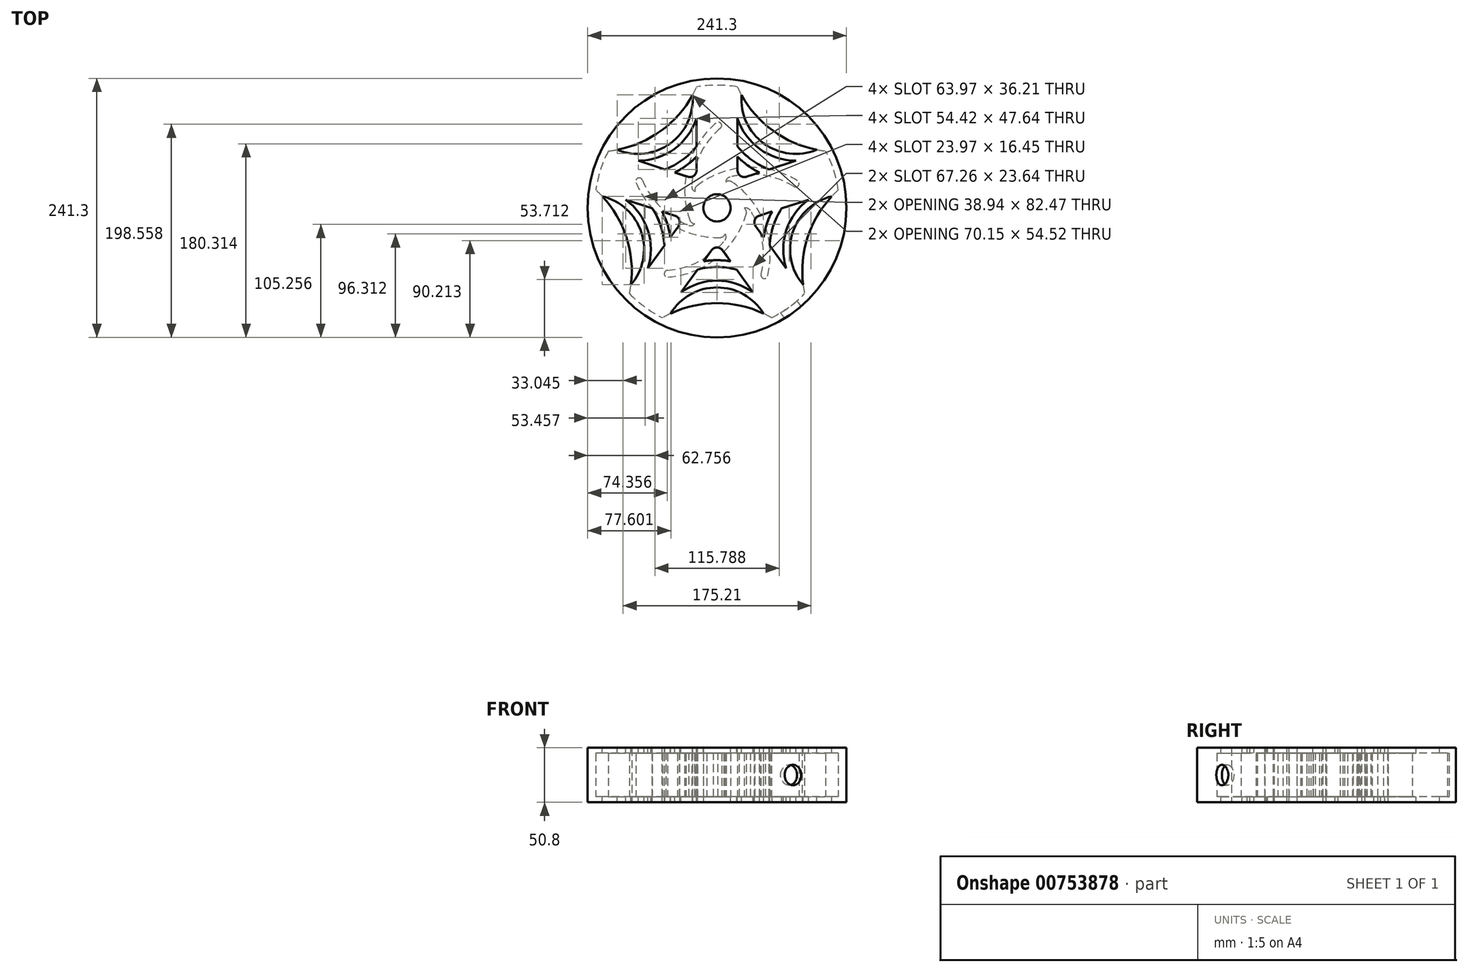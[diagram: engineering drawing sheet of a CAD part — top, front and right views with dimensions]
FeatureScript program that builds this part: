
annotation { "Feature Type Name" : "Feature", "Feature Type Description" : "" }
export const myFeature = defineFeature(function(context is Context, id is Id, definition is map)
    precondition{}
    {
        {
            var Q0;
            Q0=qCreatedBy(makeId("Top.planeOp"),FACE);
            var sketch = newSketch(context, id + "F0", { "sketchPlane" : qUnion([Q0])});
            skCircle(sketch, "E0", {"center": v(0, 0) * mm, "radius": 120.65 * mm});
            skArc(sketch, "E1.0", {"start": v(50.8, -102.4) * mm, "mid": v(67.18, -92.47) * mm, "end": v(81.68, -79.95) * mm});
            skLineSegment(sketch, "E2", {"start": v(0, 0) * mm, "end": v(0, -114.3) * mm, "construction": true});
            skArc(sketch, "E3", {"start": v(50.8, -102.4) * mm, "mid": v(0, -88.78) * mm, "end": v(-50.8, -102.4) * mm});
            skLineSegment(sketch, "E4", {"start": v(50.8, -102.4) * mm, "end": v(0, -102.4) * mm, "construction": true});
            skLineSegment(sketch, "E5", {"start": v(0, -102.4) * mm, "end": v(-50.8, -102.4) * mm, "construction": true});
            skArc(sketch, "E6.1.0", {"start": v(113.08, 16.67) * mm, "mid": v(84.43, -27.43) * mm, "end": v(81.68, -79.95) * mm});
            skArc(sketch, "E6.2.0", {"start": v(19.09, 112.7) * mm, "mid": v(52.18, 71.82) * mm, "end": v(101.28, 52.98) * mm});
            skArc(sketch, "E6.3.0", {"start": v(-101.28, 52.98) * mm, "mid": v(-52.18, 71.82) * mm, "end": v(-19.09, 112.7) * mm});
            skArc(sketch, "E6.4.0", {"start": v(-81.68, -79.95) * mm, "mid": v(-84.43, -27.43) * mm, "end": v(-113.08, 16.67) * mm});
            skArc(sketch, "E7.trimOffspring", {"start": v(113.08, 16.67) * mm, "mid": v(108.7, 35.32) * mm, "end": v(101.28, 52.98) * mm});
            skArc(sketch, "E8.trimOffspring", {"start": v(-81.68, -79.95) * mm, "mid": v(-67.18, -92.47) * mm, "end": v(-50.8, -102.4) * mm});
            skArc(sketch, "E9.trimOffspring", {"start": v(-101.28, 52.98) * mm, "mid": v(-108.7, 35.32) * mm, "end": v(-113.08, 16.67) * mm});
            skArc(sketch, "E10.trimOffspring", {"start": v(19.09, 112.7) * mm, "mid": v(0, 114.3) * mm, "end": v(-19.09, 112.7) * mm});
            skSolve(sketch);
        }
        {
            var Q0;
            Q0=makeQuery(id+"F0.imprint","IMPRINT",FACE,{"disambiguationData":[TD([[makeQuery(id+"F0.imprint","IMPRINT",EDGE,{"derivedFrom":sQuery(id+"F0.wireOp",EDGE,"E1.0")}),1.0]])]});
            var Q1;
            Q1=makeQuery(id+"F0.imprint","IMPRINT",FACE,{"disambiguationData":[TD([[makeQuery(id+"F0.imprint","IMPRINT",EDGE,{"derivedFrom":sQuery(id+"F0.wireOp",EDGE,"E0")}),1.0]])]});
            extrude(context, id + "F1", {"entities" : qUnion([Q0, Q1]), "depth" : 50.8 * mm, "offsetDistance" : 25.4 * mm, "symmetric" : true});
        }
        {
            var Q0;
            Q0=makeQuery(id+"F0.imprint","IMPRINT",FACE,{"disambiguationData":[TD([[makeQuery(id+"F0.imprint","IMPRINT",EDGE,{"derivedFrom":sQuery(id+"F0.wireOp",EDGE,"E1.0")}),1.0]])]});
            extrude(context, id + "F2", {"entities" : qUnion([Q0]), "operationType" : NewBodyOperationType.REMOVE, "depth" : 40.64 * mm, "offsetDistance" : 25.4 * mm, "symmetric" : true});
        }
        {
            var Q0;
            Q0=makeQuery(id+"F1.opExtrude","CAP_FACE",FACE,{"disambiguationData":[OSD([sQuery(id+"F0.wireOp",EDGE,"E0")])],"isStart":false});
            var sketch = newSketch(context, id + "F3", { "sketchPlane" : qUnion([Q0])});
            skCircle(sketch, "E11", {"center": v(0, 0) * mm, "radius": 12.7 * mm});
            skSolve(sketch);
        }
        {
            var Q0;
            Q0=makeQuery(id+"F3.imprint","IMPRINT",FACE,{"disambiguationData":[TD([[makeQuery(id+"F3.imprint","IMPRINT",EDGE,{"derivedFrom":sQuery(id+"F3.wireOp",EDGE,"E11")}),1.0]])]});
            extrude(context, id + "F4", {"entities" : qUnion([Q0]), "operationType" : NewBodyOperationType.REMOVE, "oppositeDirection" : true, "depth" : 25.4 * mm, "offsetDistance" : 25.4 * mm});
        }
        {
            var Q0;
            Q0=makeQuery(id+"F2.boolean.opBoolean","COPY",VERTEX,{"derivedFrom":makeQuery(id+"F2.opExtrude","CAP_VERTEX",VERTEX,{"disambiguationData":[OSD([sQuery(id+"F0.wireOp",EDGE,"E1.0"),sQuery(id+"F0.wireOp",EDGE,"E3")])],"isStart":true})});
            var Q1;
            Q1=makeQuery(id+"F2.boolean.opBoolean","COPY",VERTEX,{"derivedFrom":makeQuery(id+"F2.opExtrude","CAP_VERTEX",VERTEX,{"disambiguationData":[OSD([sQuery(id+"F0.wireOp",EDGE,"E1.0"),sQuery(id+"F0.wireOp",EDGE,"E6.1.0")])],"isStart":true})});
            var Q2;
            Q2=makeQuery(id+"F2.boolean.opBoolean","COPY",VERTEX,{"derivedFrom":makeQuery(id+"F2.opExtrude","CAP_VERTEX",VERTEX,{"disambiguationData":[OSD([sQuery(id+"F0.wireOp",EDGE,"E1.0"),sQuery(id+"F0.wireOp",EDGE,"E6.1.0")])],"isStart":false})});
            cPlane(context, id + "F5", {"entities" : qUnion([Q0, Q1, Q2]), "cplaneType" : CPlaneType.THREE_POINT, "offset" : 25.4 * mm, "width" : 152.4 * mm, "height" : 152.4 * mm});
        }
        {
            var Q0;
            Q0=qCreatedBy(id+"F5.planeOp",FACE);
            var sketch = newSketch(context, id + "F6", { "sketchPlane" : qUnion([Q0])});
            skCircle(sketch, "E12", {"center": v(0, 0) * mm, "radius": 9.53 * mm});
            skSolve(sketch);
        }
        {
            var Q0;
            Q0 = qSketchRegion(id + "F6", true);
            extrude(context, id + "F7", {"entities" : qUnion([Q0]), "operationType" : NewBodyOperationType.REMOVE, "oppositeDirection" : true, "depth" : 25.4 * mm, "offsetDistance" : 25.4 * mm});
        }
        {
            var Q0;
            Q0=qCreatedBy(makeId("Top.planeOp"),FACE);
            var sketch = newSketch(context, id + "F8", { "sketchPlane" : qUnion([Q0])});
            skCircle(sketch, "E13", {"center": v(0, 0) * mm, "radius": 12.7 * mm});
            skArc(sketch, "E14.0", {"start": v(7.62, -24.23) * mm, "mid": v(10.53, -23.11) * mm, "end": v(13.29, -21.65) * mm});
            skLineSegment(sketch, "E15", {"start": v(13.29, -21.65) * mm, "end": v(-81.68, -79.95) * mm, "construction": true});
            skArc(sketch, "E16", {"start": v(-46.24, -58.2) * mm, "mid": v(-12.04, -47.14) * mm, "end": v(13.29, -21.65) * mm});
            skArc(sketch, "E17.0", {"start": v(-45.76, -64.52) * mm, "mid": v(2.06, -44.67) * mm, "end": v(28.65, -0.24) * mm});
            skLineSegment(sketch, "E18", {"start": v(28.65, -0.24) * mm, "end": v(25.4, -0.24) * mm});
            skArc(sketch, "E19", {"start": v(-46.24, -58.2) * mm, "mid": v(-49.17, -61.6) * mm, "end": v(-45.76, -64.52) * mm});
            skArc(sketch, "E20.1.0", {"start": v(41.06, -61.96) * mm, "mid": v(43.39, -65.8) * mm, "end": v(47.23, -63.46) * mm});
            skArc(sketch, "E20.1.1", {"start": v(41.06, -61.96) * mm, "mid": v(41.11, -26.02) * mm, "end": v(24.7, 5.95) * mm});
            skArc(sketch, "E20.1.2", {"start": v(47.23, -63.46) * mm, "mid": v(43.12, -11.85) * mm, "end": v(9.08, 27.17) * mm});
            skLineSegment(sketch, "E20.1.3", {"start": v(9.08, 27.17) * mm, "end": v(8.08, 24.08) * mm});
            skArc(sketch, "E20.2.0", {"start": v(71.61, 19.9) * mm, "mid": v(75.98, 20.93) * mm, "end": v(74.95, 25.3) * mm});
            skArc(sketch, "E20.2.1", {"start": v(71.61, 19.9) * mm, "mid": v(37.45, 31.06) * mm, "end": v(1.97, 25.32) * mm});
            skArc(sketch, "E20.2.2", {"start": v(74.95, 25.3) * mm, "mid": v(24.6, 37.35) * mm, "end": v(-23.03, 17.03) * mm});
            skLineSegment(sketch, "E20.2.3", {"start": v(-23.03, 17.03) * mm, "end": v(-20.4, 15.12) * mm});
            skArc(sketch, "E20.3.0", {"start": v(3.2, 74.26) * mm, "mid": v(3.57, 78.73) * mm, "end": v(-0.9, 79.1) * mm});
            skArc(sketch, "E20.3.1", {"start": v(3.2, 74.26) * mm, "mid": v(-17.97, 45.21) * mm, "end": v(-23.47, 9.7) * mm});
            skArc(sketch, "E20.3.2", {"start": v(-0.9, 79.1) * mm, "mid": v(-27.92, 34.93) * mm, "end": v(-23.32, -16.64) * mm});
            skLineSegment(sketch, "E20.3.3", {"start": v(-23.32, -16.64) * mm, "end": v(-20.69, -14.73) * mm});
            skArc(sketch, "E20.4.0", {"start": v(-69.63, 26) * mm, "mid": v(-73.77, 27.73) * mm, "end": v(-75.5, 23.58) * mm});
            skArc(sketch, "E20.4.1", {"start": v(-69.63, 26) * mm, "mid": v(-48.55, -3.12) * mm, "end": v(-16.48, -19.33) * mm});
            skArc(sketch, "E20.4.2", {"start": v(-75.5, 23.58) * mm, "mid": v(-41.85, -15.76) * mm, "end": v(8.62, -27.32) * mm});
            skLineSegment(sketch, "E20.4.3", {"start": v(8.62, -27.32) * mm, "end": v(7.62, -24.23) * mm});
            skArc(sketch, "E21.trimOffspring", {"start": v(-20.69, -14.73) * mm, "mid": v(-18.73, -17.16) * mm, "end": v(-16.48, -19.33) * mm});
            skArc(sketch, "E22.trimOffspring", {"start": v(-20.4, 15.12) * mm, "mid": v(-22.1, 12.5) * mm, "end": v(-23.47, 9.7) * mm});
            skArc(sketch, "E23.trimOffspring", {"start": v(8.08, 24.08) * mm, "mid": v(5.06, 24.9) * mm, "end": v(1.97, 25.32) * mm});
            skArc(sketch, "E24.trimOffspring", {"start": v(25.4, -0.24) * mm, "mid": v(25.24, 2.88) * mm, "end": v(24.7, 5.95) * mm});
            skSolve(sketch);
        }
        {
            var Q0;
            Q0 = qSketchRegion(id + "F8", true);
            extrude(context, id + "F9", {"entities" : qUnion([Q0]), "depth" : 40.64 * mm, "offsetDistance" : 25.4 * mm, "symmetric" : true});
        }
        {
            var Q0;
            Q0=makeQuery(id+"F9.opExtrude","SWEPT_EDGE",EDGE,{"disambiguationData":[OSD([sQuery(id+"F8.wireOp",EDGE,"E20.2.2"),sQuery(id+"F8.wireOp",EDGE,"E20.2.3")])]});
            var Q1;
            Q1=makeQuery(id+"F9.opExtrude","SWEPT_EDGE",EDGE,{"disambiguationData":[OSD([sQuery(id+"F8.wireOp",EDGE,"E20.3.1"),sQuery(id+"F8.wireOp",EDGE,"E22.trimOffspring")])]});
            var Q2;
            Q2=makeQuery(id+"F9.opExtrude","SWEPT_EDGE",EDGE,{"disambiguationData":[OSD([sQuery(id+"F8.wireOp",EDGE,"E20.3.2"),sQuery(id+"F8.wireOp",EDGE,"E20.3.3")])]});
            var Q3;
            Q3=makeQuery(id+"F9.opExtrude","SWEPT_EDGE",EDGE,{"disambiguationData":[OSD([sQuery(id+"F8.wireOp",EDGE,"E20.4.2"),sQuery(id+"F8.wireOp",EDGE,"E20.4.3")])]});
            var Q4;
            Q4=makeQuery(id+"F9.opExtrude","SWEPT_EDGE",EDGE,{"disambiguationData":[OSD([sQuery(id+"F8.wireOp",EDGE,"E17.0"),sQuery(id+"F8.wireOp",EDGE,"E18")])]});
            var Q5;
            Q5=makeQuery(id+"F9.opExtrude","SWEPT_EDGE",EDGE,{"disambiguationData":[OSD([sQuery(id+"F8.wireOp",EDGE,"E20.1.2"),sQuery(id+"F8.wireOp",EDGE,"E20.1.3")])]});
            var Q6;
            Q6=makeQuery(id+"F9.opExtrude","SWEPT_EDGE",EDGE,{"disambiguationData":[OSD([sQuery(id+"F8.wireOp",EDGE,"E20.4.1"),sQuery(id+"F8.wireOp",EDGE,"E21.trimOffspring")])]});
            var Q7;
            Q7=makeQuery(id+"F9.opExtrude","SWEPT_EDGE",EDGE,{"disambiguationData":[OSD([sQuery(id+"F8.wireOp",EDGE,"E14.0"),sQuery(id+"F8.wireOp",EDGE,"E16")])]});
            var Q8;
            Q8=makeQuery(id+"F9.opExtrude","SWEPT_EDGE",EDGE,{"disambiguationData":[OSD([sQuery(id+"F8.wireOp",EDGE,"E20.1.1"),sQuery(id+"F8.wireOp",EDGE,"E24.trimOffspring")])]});
            var Q9;
            Q9=makeQuery(id+"F9.opExtrude","SWEPT_EDGE",EDGE,{"disambiguationData":[OSD([sQuery(id+"F8.wireOp",EDGE,"E20.2.1"),sQuery(id+"F8.wireOp",EDGE,"E23.trimOffspring")])]});
            fillet(context, id + "F10", {"entities" : qUnion([Q0, Q1, Q2, Q3, Q4, Q5, Q6, Q7, Q8, Q9]), "radius" : 5.08 * mm, "tangentPropagation" : true, "allowEdgeOverflow" : false});
        }
        {
            var Q0;
            Q0=qCreatedBy(makeId("Top.planeOp"),FACE);
            var sketch = newSketch(context, id + "F11", { "sketchPlane" : qUnion([Q0])});
            skLineSegment(sketch, "E25", {"start": v(-5.14, -39.54) * mm, "end": v(-12.6, -49.82) * mm});
            skLineSegment(sketch, "E26.1.1", {"start": v(5.14, -39.54) * mm, "end": v(12.6, -49.82) * mm});
            skPoint(sketch, "E27.visualSharp", {"position": v(0, -32.47) * mm});
            skArc(sketch, "E27.filletArc", {"start": v(5.14, -39.54) * mm, "mid": v(0, -36.92) * mm, "end": v(-5.14, -39.54) * mm});
            skArc(sketch, "E28", {"start": v(12.6, -49.82) * mm, "mid": v(0, -48.77) * mm, "end": v(-12.6, -49.82) * mm});
            skArc(sketch, "E29.0", {"start": v(18.2, -57.53) * mm, "mid": v(0, -55.12) * mm, "end": v(-18.2, -57.53) * mm});
            skArc(sketch, "E30.0", {"start": v(33.63, -78.76) * mm, "mid": v(0, -67.82) * mm, "end": v(-33.63, -78.76) * mm});
            skArc(sketch, "E31.0", {"start": v(43.36, -98.5) * mm, "mid": v(0, -74.17) * mm, "end": v(-43.36, -98.5) * mm});
            skArc(sketch, "E32", {"start": v(43.36, -98.5) * mm, "mid": v(0, -88.78) * mm, "end": v(-43.36, -98.5) * mm});
            skLineSegment(sketch, "E33.trimOffspring", {"start": v(18.2, -57.53) * mm, "end": v(33.63, -78.76) * mm});
            skLineSegment(sketch, "E34.trimOffspring", {"start": v(-18.2, -57.53) * mm, "end": v(-33.63, -78.76) * mm});
            skArc(sketch, "E35.1.0", {"start": v(107.07, 10.8) * mm, "mid": v(84.43, -27.43) * mm, "end": v(80.28, -71.67) * mm});
            skArc(sketch, "E35.1.1", {"start": v(107.07, 10.8) * mm, "mid": v(70.54, -22.92) * mm, "end": v(80.28, -71.67) * mm});
            skArc(sketch, "E35.1.2", {"start": v(85.3, 7.65) * mm, "mid": v(64.5, -20.96) * mm, "end": v(64.51, -56.32) * mm});
            skLineSegment(sketch, "E35.1.3", {"start": v(60.34, -0.46) * mm, "end": v(85.3, 7.65) * mm});
            skLineSegment(sketch, "E35.1.4", {"start": v(49.09, -35.1) * mm, "end": v(64.51, -56.32) * mm});
            skArc(sketch, "E35.1.5", {"start": v(60.34, -0.46) * mm, "mid": v(52.42, -17.03) * mm, "end": v(49.09, -35.1) * mm});
            skArc(sketch, "E35.1.6", {"start": v(51.27, -3.4) * mm, "mid": v(46.38, -15.07) * mm, "end": v(43.48, -27.38) * mm});
            skLineSegment(sketch, "E35.1.7", {"start": v(39.2, -7.33) * mm, "end": v(51.27, -3.4) * mm});
            skLineSegment(sketch, "E35.1.8", {"start": v(36.02, -17.1) * mm, "end": v(43.48, -27.38) * mm});
            skArc(sketch, "E35.1.9", {"start": v(39.2, -7.33) * mm, "mid": v(35.12, -11.41) * mm, "end": v(36.02, -17.1) * mm});
            skArc(sketch, "E35.2.0", {"start": v(22.82, 105.17) * mm, "mid": v(52.18, 71.82) * mm, "end": v(92.97, 54.2) * mm});
            skArc(sketch, "E35.2.1", {"start": v(22.82, 105.17) * mm, "mid": v(43.6, 60) * mm, "end": v(92.97, 54.2) * mm});
            skArc(sketch, "E35.2.2", {"start": v(19.09, 83.49) * mm, "mid": v(39.86, 54.86) * mm, "end": v(73.5, 43.95) * mm});
            skLineSegment(sketch, "E35.2.3", {"start": v(19.09, 57.25) * mm, "end": v(19.09, 83.49) * mm});
            skLineSegment(sketch, "E35.2.4", {"start": v(48.55, 35.84) * mm, "end": v(73.5, 43.95) * mm});
            skArc(sketch, "E35.2.5", {"start": v(19.09, 57.25) * mm, "mid": v(32.4, 44.6) * mm, "end": v(48.55, 35.84) * mm});
            skArc(sketch, "E35.2.6", {"start": v(19.09, 47.7) * mm, "mid": v(28.66, 39.45) * mm, "end": v(39.48, 32.9) * mm});
            skLineSegment(sketch, "E35.2.7", {"start": v(19.09, 35) * mm, "end": v(19.09, 47.7) * mm});
            skLineSegment(sketch, "E35.2.8", {"start": v(27.4, 28.97) * mm, "end": v(39.48, 32.9) * mm});
            skArc(sketch, "E35.2.9", {"start": v(19.09, 35) * mm, "mid": v(21.7, 29.87) * mm, "end": v(27.4, 28.97) * mm});
            skArc(sketch, "E35.3.0", {"start": v(-92.97, 54.2) * mm, "mid": v(-52.18, 71.82) * mm, "end": v(-22.82, 105.17) * mm});
            skArc(sketch, "E35.3.1", {"start": v(-92.97, 54.2) * mm, "mid": v(-43.6, 60) * mm, "end": v(-22.82, 105.17) * mm});
            skArc(sketch, "E35.3.2", {"start": v(-73.5, 43.95) * mm, "mid": v(-39.86, 54.86) * mm, "end": v(-19.09, 83.49) * mm});
            skLineSegment(sketch, "E35.3.3", {"start": v(-48.55, 35.84) * mm, "end": v(-73.5, 43.95) * mm});
            skLineSegment(sketch, "E35.3.4", {"start": v(-19.09, 57.25) * mm, "end": v(-19.09, 83.49) * mm});
            skArc(sketch, "E35.3.5", {"start": v(-48.55, 35.84) * mm, "mid": v(-32.4, 44.6) * mm, "end": v(-19.09, 57.25) * mm});
            skArc(sketch, "E35.3.6", {"start": v(-39.48, 32.9) * mm, "mid": v(-28.66, 39.45) * mm, "end": v(-19.09, 47.7) * mm});
            skLineSegment(sketch, "E35.3.7", {"start": v(-27.4, 28.97) * mm, "end": v(-39.48, 32.9) * mm});
            skLineSegment(sketch, "E35.3.8", {"start": v(-19.09, 35) * mm, "end": v(-19.09, 47.7) * mm});
            skArc(sketch, "E35.3.9", {"start": v(-27.4, 28.97) * mm, "mid": v(-21.7, 29.87) * mm, "end": v(-19.09, 35) * mm});
            skArc(sketch, "E35.4.0", {"start": v(-80.28, -71.67) * mm, "mid": v(-84.43, -27.43) * mm, "end": v(-107.07, 10.8) * mm});
            skArc(sketch, "E35.4.1", {"start": v(-80.28, -71.67) * mm, "mid": v(-70.54, -22.92) * mm, "end": v(-107.07, 10.8) * mm});
            skArc(sketch, "E35.4.2", {"start": v(-64.51, -56.32) * mm, "mid": v(-64.5, -20.96) * mm, "end": v(-85.3, 7.65) * mm});
            skLineSegment(sketch, "E35.4.3", {"start": v(-49.09, -35.1) * mm, "end": v(-64.51, -56.32) * mm});
            skLineSegment(sketch, "E35.4.4", {"start": v(-60.34, -0.46) * mm, "end": v(-85.3, 7.65) * mm});
            skArc(sketch, "E35.4.5", {"start": v(-49.09, -35.1) * mm, "mid": v(-52.42, -17.03) * mm, "end": v(-60.34, -0.46) * mm});
            skArc(sketch, "E35.4.6", {"start": v(-43.48, -27.38) * mm, "mid": v(-46.38, -15.07) * mm, "end": v(-51.27, -3.4) * mm});
            skLineSegment(sketch, "E35.4.7", {"start": v(-36.02, -17.1) * mm, "end": v(-43.48, -27.38) * mm});
            skLineSegment(sketch, "E35.4.8", {"start": v(-39.2, -7.33) * mm, "end": v(-51.27, -3.4) * mm});
            skArc(sketch, "E35.4.9", {"start": v(-36.02, -17.1) * mm, "mid": v(-35.12, -11.41) * mm, "end": v(-39.2, -7.33) * mm});
            skPoint(sketch, "E35.center", {"position": v(0, 0) * mm});
            skSolve(sketch);
        }
        {
            var Q0;
            Q0 = qSketchRegion(id + "F11", true);
            extrude(context, id + "F12", {"entities" : qUnion([Q0]), "operationType" : NewBodyOperationType.REMOVE, "oppositeDirection" : true, "depth" : 76.2 * mm, "offsetDistance" : 25.4 * mm, "symmetric" : true});
        }
    });
